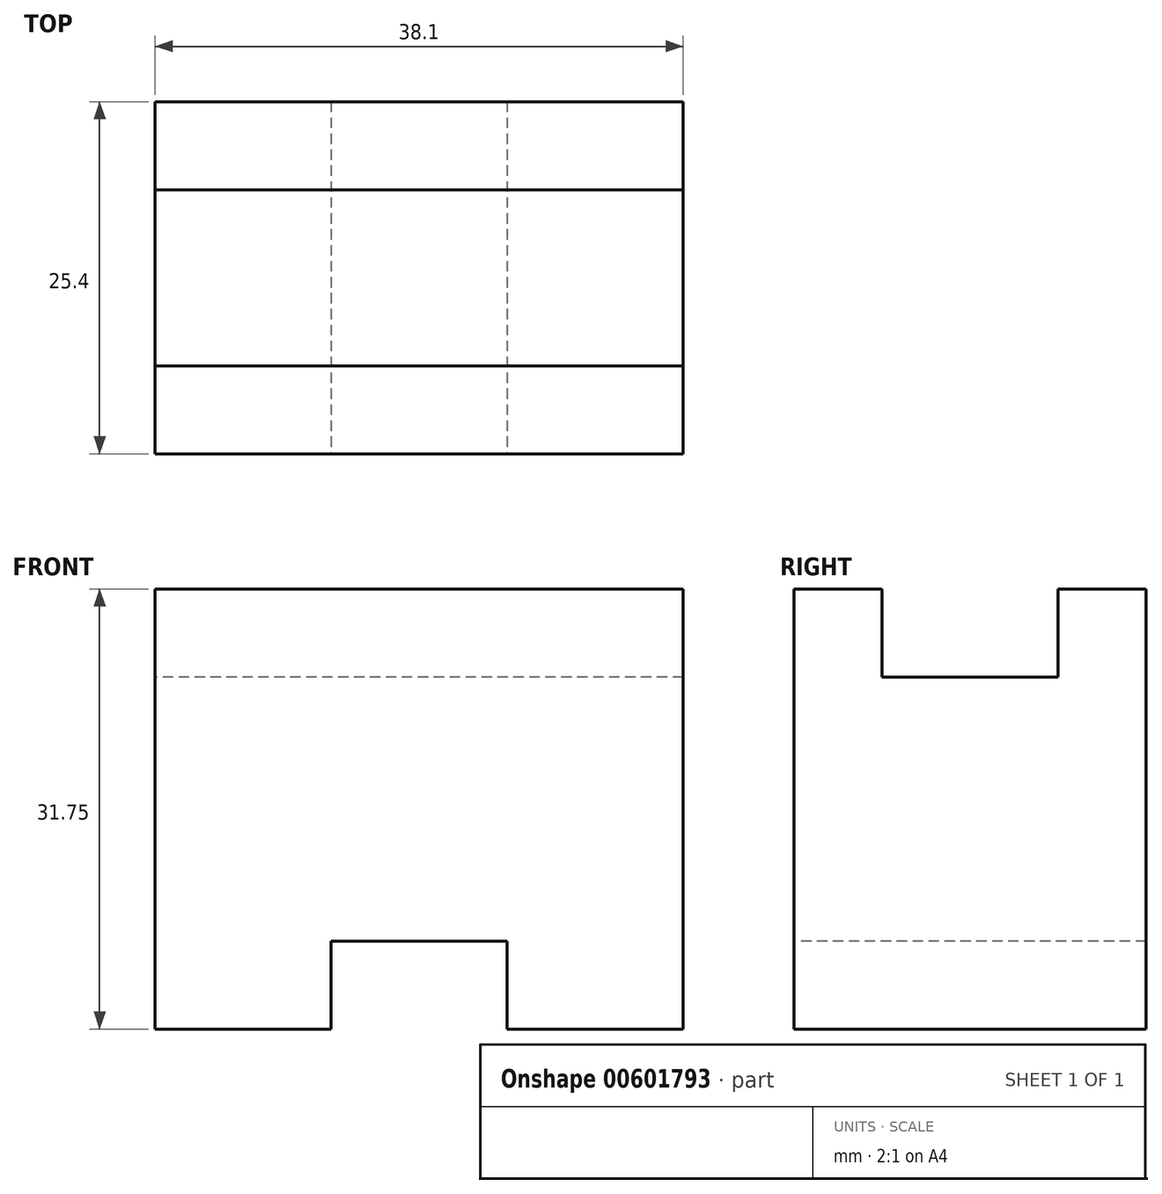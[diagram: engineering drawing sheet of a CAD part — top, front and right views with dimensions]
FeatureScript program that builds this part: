
annotation { "Feature Type Name" : "Feature", "Feature Type Description" : "" }
export const myFeature = defineFeature(function(context is Context, id is Id, definition is map)
    precondition{}
    {
        {
            var Q0;
            Q0=qCreatedBy(makeId("Right.planeOp"),FACE);
            var sketch = newSketch(context, id + "F0", { "sketchPlane" : qUnion([Q0])});
            skLineSegment(sketch, "E0", {"start": v(0, 0) * mm, "end": v(0, 31.75) * mm});
            skLineSegment(sketch, "E1", {"start": v(0, 31.75) * mm, "end": v(6.35, 31.75) * mm});
            skLineSegment(sketch, "E2", {"start": v(6.35, 31.75) * mm, "end": v(6.35, 25.4) * mm});
            skLineSegment(sketch, "E3", {"start": v(6.35, 25.4) * mm, "end": v(19.05, 25.4) * mm});
            skLineSegment(sketch, "E4", {"start": v(19.05, 25.4) * mm, "end": v(19.05, 31.75) * mm});
            skLineSegment(sketch, "E5", {"start": v(19.05, 31.75) * mm, "end": v(25.4, 31.75) * mm});
            skLineSegment(sketch, "E6", {"start": v(25.4, 31.75) * mm, "end": v(25.4, 0) * mm});
            skLineSegment(sketch, "E7", {"start": v(25.4, 0) * mm, "end": v(0, 0) * mm});
            skSolve(sketch);
        }
        {
            var Q0;
            Q0=makeQuery(id+"F0.imprint","IMPRINT",FACE,{"disambiguationData":[TD([[makeQuery(id+"F0.imprint","IMPRINT",EDGE,{"derivedFrom":sQuery(id+"F0.wireOp",EDGE,"E0")}),-1.0]])]});
            extrude(context, id + "F1", {"entities" : qUnion([Q0]), "depth" : 38.1 * mm, "offsetDistance" : 25.4 * mm});
        }
        {
            var Q0;
            Q0=qCreatedBy(makeId("Front.planeOp"),FACE);
            var sketch = newSketch(context, id + "F2", { "sketchPlane" : qUnion([Q0])});
            skLineSegment(sketch, "E8", {"start": v(0, 0) * mm, "end": v(12.7, 0) * mm});
            skLineSegment(sketch, "E9", {"start": v(12.7, 0) * mm, "end": v(12.7, 6.35) * mm});
            skLineSegment(sketch, "E10", {"start": v(12.7, 6.35) * mm, "end": v(25.4, 6.35) * mm});
            skLineSegment(sketch, "E11", {"start": v(25.4, 6.35) * mm, "end": v(25.4, 0) * mm});
            skLineSegment(sketch, "E12", {"start": v(25.4, 0) * mm, "end": v(38.1, 0) * mm});
            skLineSegment(sketch, "E13.bottom", {"start": v(12.7, 0) * mm, "end": v(25.4, 0) * mm});
            skLineSegment(sketch, "E13.right", {"start": v(25.4, 0) * mm, "end": v(25.4, 6.35) * mm});
            skSolve(sketch);
        }
        {
            var Q0;
            Q0 = qSketchRegion(id + "F2", true);
            extrude(context, id + "F3", {"entities" : qUnion([Q0]), "operationType" : NewBodyOperationType.REMOVE, "oppositeDirection" : true, "depth" : 25.4 * mm, "offsetDistance" : 25.4 * mm});
        }
    });
